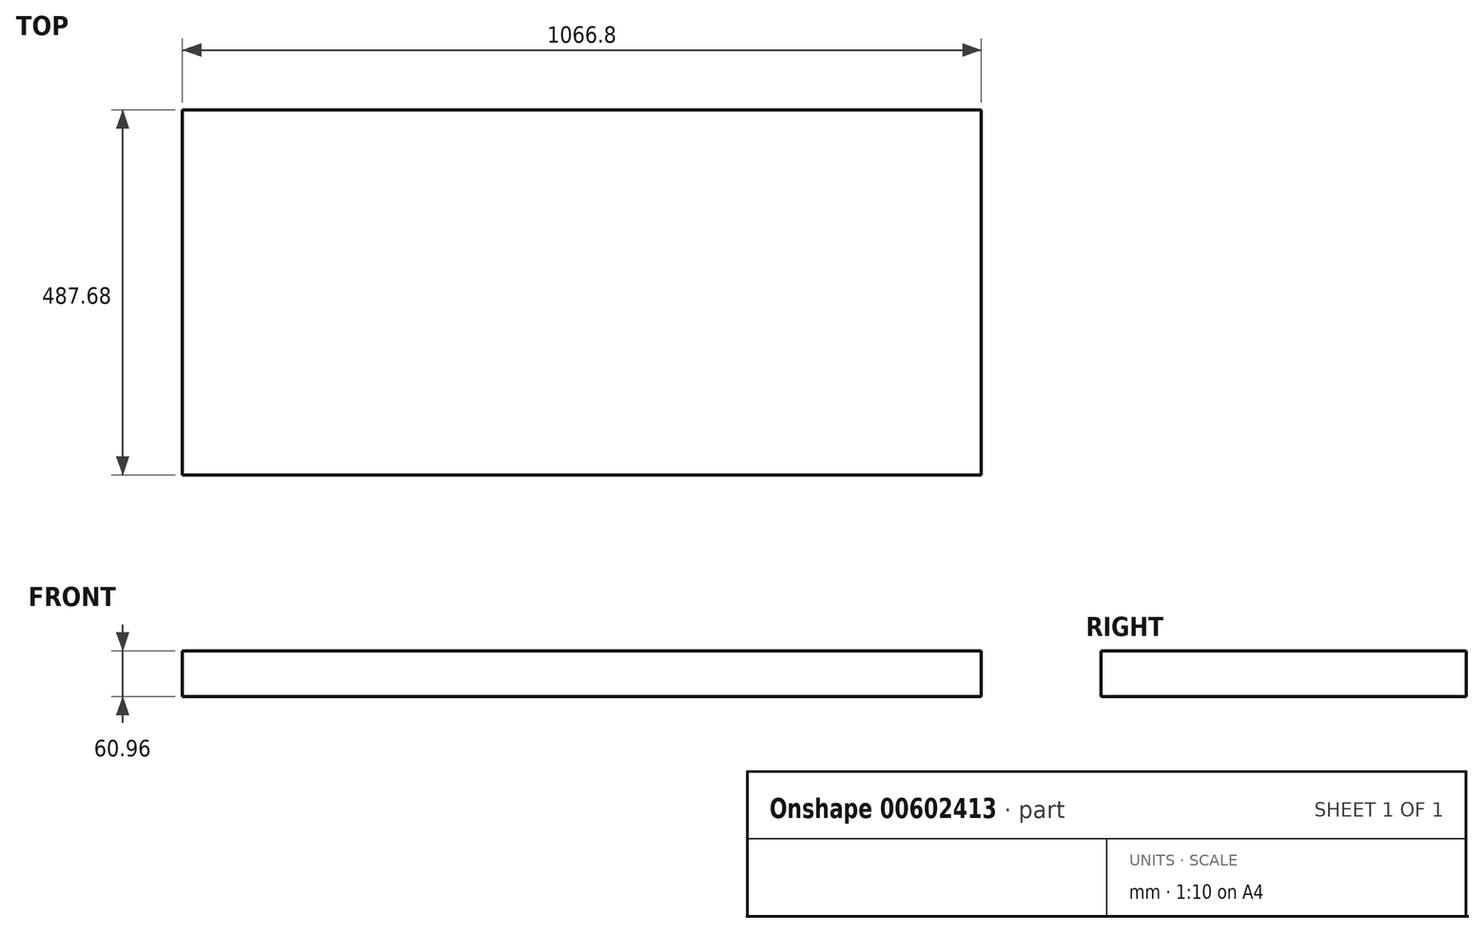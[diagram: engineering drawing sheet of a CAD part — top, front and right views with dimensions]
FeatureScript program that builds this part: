
annotation { "Feature Type Name" : "Feature", "Feature Type Description" : "" }
export const myFeature = defineFeature(function(context is Context, id is Id, definition is map)
    precondition{}
    {
        {
            var Q0;
            Q0=qCreatedBy(makeId("Top.planeOp"),FACE);
            var sketch = newSketch(context, id + "F0", { "sketchPlane" : qUnion([Q0])});
            skLineSegment(sketch, "E0.bottom", {"start": v(0, 0) * mm, "end": v(1066.8, 0) * mm});
            skLineSegment(sketch, "E0.top", {"start": v(0, -487.68) * mm, "end": v(1066.8, -487.68) * mm});
            skLineSegment(sketch, "E0.left", {"start": v(0, 0) * mm, "end": v(0, -487.68) * mm});
            skLineSegment(sketch, "E0.right", {"start": v(1066.8, 0) * mm, "end": v(1066.8, -487.68) * mm});
            skSolve(sketch);
        }
        {
            var Q0;
            Q0=makeQuery(id+"F0.imprint","IMPRINT",FACE,{"disambiguationData":[TD([[makeQuery(id+"F0.imprint","IMPRINT",EDGE,{"derivedFrom":sQuery(id+"F0.wireOp",EDGE,"E0.bottom")}),-1.0]])]});
            extrude(context, id + "F1", {"entities" : qUnion([Q0]), "depth" : 60.96 * mm, "offsetDistance" : 30.48 * mm});
        }
    });
